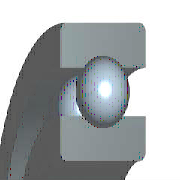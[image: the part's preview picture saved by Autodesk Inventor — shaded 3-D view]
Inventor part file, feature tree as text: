
AUTODESK INVENTOR PART (.ipt)
format: ipt  version: 2023.2 (Build 272271030, 271C)  size: 335,872 bytes
history: native  units: mm (DEFAULTED — no unit token found)
features: sketch x5, other x3, plane x2, pattern_circular x1, fillet x1
ambient origin geometry x8: Origin, YZ Plane, XZ Plane, XY Plane, X Axis, Y Axis, Z Axis, Center Point
bodies: Solid1 (feature_tree)
feature tree (12):
  sketch  "Sketch1"  dims[d2=72.0mm]
  other  "WorkPoint1"
  other  "WorkAxis1"
  plane  "WorkPlane3"
  plane  "WorkPlane4"
  sketch  "Sketch4"  dims[d5=17.0mm]
  other  "WorkPoint2"
  pattern_circular  "PolarArray1"  Count=2  [1 undecoded]
  fillet  "Fillet1"  Radius=35.0mm
  sketch  "Sketch2"  dims[d3=72.0mm]
  sketch  "Sketch3"  dims[d4=19.0mm]
  sketch  "Sketch5"  dims[d6=360.0deg d7=0.0mm d8=15.6mm d9=11.1mm d10=360.0deg d11=-17.0mm d12=0.0mm d13=0.0mm d14=15.6001mm d15=11.1001mm d16=360.0deg d17=76.297297mm d19=360.0deg d20=1.1mm d21=23.42mm d22=26.75mm d23=30.08mm d26=0.0mm d27=0.0mm d28=0.0mm d29=0.0mm d30=0.0mm]
note: 1 required parameter value undecoded (feature->parameter linkage not recoverable at this tier; creation-order binding heuristic only, values carry confidence <= 0.55)
